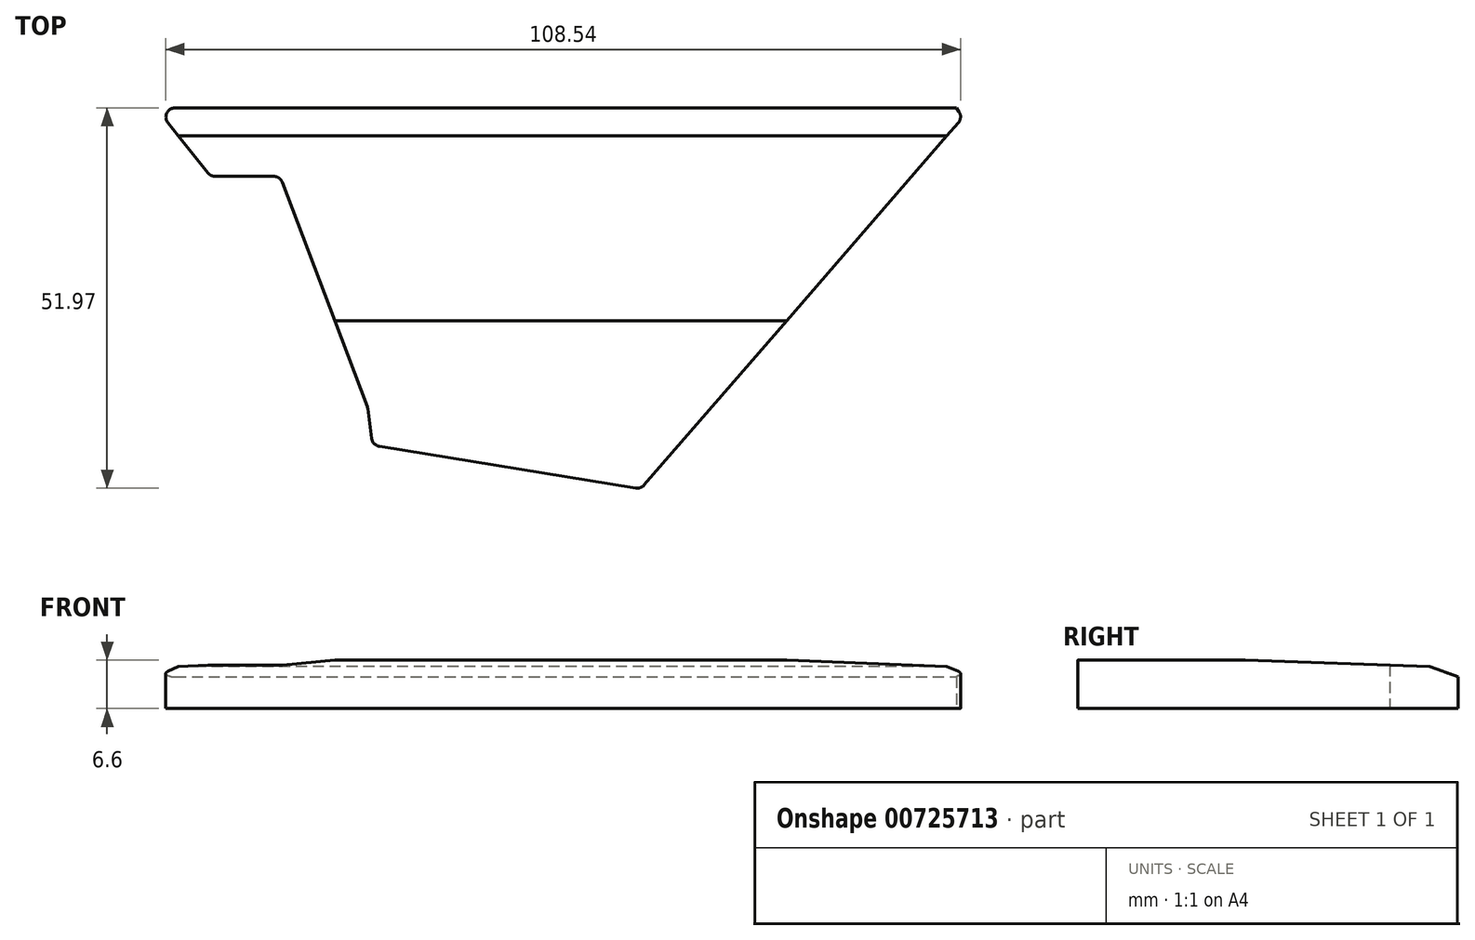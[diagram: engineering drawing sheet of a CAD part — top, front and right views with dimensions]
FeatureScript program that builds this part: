
annotation { "Feature Type Name" : "Feature", "Feature Type Description" : "" }
export const myFeature = defineFeature(function(context is Context, id is Id, definition is map)
    precondition{}
    {
        {
            var Q0;
            Q0=qCreatedBy(makeId("Top.planeOp"),FACE);
            var sketch = newSketch(context, id + "F0", { "sketchPlane" : qUnion([Q0])});
            skLineSegment(sketch, "E0", {"start": v(-45.3, 26.52) * mm, "end": v(-37.83, 17.16) * mm});
            skLineSegment(sketch, "E1", {"start": v(-37.83, 17.16) * mm, "end": v(-28.34, 17.16) * mm});
            skLineSegment(sketch, "E2", {"start": v(-28.34, 17.16) * mm, "end": v(-16.38, -14.46) * mm});
            skLineSegment(sketch, "E3", {"start": v(-16.38, -14.46) * mm, "end": v(-15.72, -19.57) * mm});
            skLineSegment(sketch, "E4", {"start": v(-15.72, -19.57) * mm, "end": v(20.94, -25.55) * mm});
            skLineSegment(sketch, "E5", {"start": v(-45.3, 26.52) * mm, "end": v(91.34, 26.52) * mm});
            skLineSegment(sketch, "E6", {"start": v(20.94, -25.55) * mm, "end": v(66.09, 26.52) * mm});
            skLineSegment(sketch, "E7", {"start": v(64.03, 26.52) * mm, "end": v(64.93, 25.18) * mm});
            skSolve(sketch);
        }
        {
            var Q0;
            {var subQ0=sQuery(id+"F0.wireOp",EDGE,"E0");Q0=makeQuery(id+"F0.imprint","IMPRINT",FACE,{"disambiguationData":[TD([[makeQuery(id+"F0.imprint","IMPRINT",EDGE,{"derivedFrom":subQ0}),1.0]])]});}
            extrude(context, id + "F1", {"entities" : qUnion([Q0]), "depth" : 6.6 * mm, "offsetDistance" : 25.4 * mm});
        }
        {
            var Q0;
            Q0=makeQuery(id+"F1.opExtrude","CAP_EDGE",EDGE,{"disambiguationData":[OSD([sQuery(id+"F0.wireOp",EDGE,"E5")])],"isStart":false});
            chamfer(context, id + "F2", {"entities" : qUnion([Q0]), "chamferType" : ChamferType.OFFSET_ANGLE, "width" : 0.5 * mm, "oppositeDirection" : false, "angle" : 89 * degree, "tangentPropagation" : true});
        }
        {
            var Q0;
            {var subQ0=sQuery(id+"F0.wireOp",EDGE,"E5");Q0=makeQuery(id+"F2.opChamfer","BLEND_EDGE",EDGE,{"blendedFrom":[makeQuery(id+"F1.opExtrude","CAP_EDGE",EDGE,{"disambiguationData":[OSD([subQ0])],"isStart":false}),makeQuery(id+"F1.opExtrude","SWEPT_FACE",FACE,{"disambiguationData":[OSD([subQ0])]})],"blendedInto":[makeQuery(id+"F1.opExtrude","SWEPT_FACE",FACE,{"disambiguationData":[OSD([subQ0])]})]});}
            chamfer(context, id + "F3", {"entities" : qUnion([Q0]), "chamferType" : ChamferType.OFFSET_ANGLE, "width" : 0.5 * mm, "oppositeDirection" : false, "angle" : 88 * degree, "tangentPropagation" : true});
        }
        {
            var Q0;
            {var subQ0=sQuery(id+"F0.wireOp",EDGE,"E5");var subQ1=makeQuery(id+"F1.opExtrude","SWEPT_FACE",FACE,{"disambiguationData":[OSD([subQ0])]});Q0=makeQuery(id+"F3.opChamfer","BLEND_EDGE",EDGE,{"blendedFrom":[makeQuery(id+"F2.opChamfer","BLEND_EDGE",EDGE,{"blendedFrom":[makeQuery(id+"F1.opExtrude","CAP_EDGE",EDGE,{"disambiguationData":[OSD([subQ0])],"isStart":false}),subQ1],"blendedInto":[subQ1]}),subQ1],"blendedInto":[subQ1]});}
            chamfer(context, id + "F4", {"entities" : qUnion([Q0]), "chamferType" : ChamferType.OFFSET_ANGLE, "width" : 1.27 * mm, "oppositeDirection" : false, "angle" : 70 * degree, "tangentPropagation" : true});
        }
        {
            var Q0;
            Q0=makeQuery(id+"F1.opExtrude","SWEPT_EDGE",EDGE,{"disambiguationData":[OSD([sQuery(id+"F0.wireOp",EDGE,"E0"),sQuery(id+"F0.wireOp",EDGE,"E5")])]});
            var Q1;
            Q1=makeQuery(id+"F1.opExtrude","SWEPT_EDGE",EDGE,{"disambiguationData":[OSD([sQuery(id+"F0.wireOp",EDGE,"E0"),sQuery(id+"F0.wireOp",EDGE,"E1")])]});
            var Q2;
            Q2=makeQuery(id+"F1.opExtrude","SWEPT_EDGE",EDGE,{"disambiguationData":[OSD([sQuery(id+"F0.wireOp",EDGE,"E1"),sQuery(id+"F0.wireOp",EDGE,"E2")])]});
            var Q3;
            Q3=makeQuery(id+"F1.opExtrude","SWEPT_EDGE",EDGE,{"disambiguationData":[OSD([sQuery(id+"F0.wireOp",EDGE,"E2"),sQuery(id+"F0.wireOp",EDGE,"E3")])]});
            var Q4;
            Q4=makeQuery(id+"F1.opExtrude","SWEPT_EDGE",EDGE,{"disambiguationData":[OSD([sQuery(id+"F0.wireOp",EDGE,"E3"),sQuery(id+"F0.wireOp",EDGE,"E4")])]});
            var Q5;
            Q5=makeQuery(id+"F1.opExtrude","SWEPT_EDGE",EDGE,{"disambiguationData":[OSD([sQuery(id+"F0.wireOp",EDGE,"E4"),sQuery(id+"F0.wireOp",EDGE,"E6")])]});
            var Q6;
            Q6=makeQuery(id+"F1.opExtrude","SWEPT_EDGE",EDGE,{"disambiguationData":[OSD([sQuery(id+"F0.wireOp",EDGE,"E6"),sQuery(id+"F0.wireOp",EDGE,"E7")])]});
            fillet(context, id + "F5", {"entities" : qUnion([Q0, Q1, Q2, Q3, Q4, Q5, Q6]), "radius" : 1.27 * mm, "tangentPropagation" : true, "allowEdgeOverflow" : false});
        }
    });
